FCSTD DOCUMENT  (FreeCAD 1.1R14555 (Git shallow))
Label: generated_example_K93-10436_all7
License: All rights reserved
LicenseURL: https://en.wikipedia.org/wiki/All_rights_reserved
objects: App::FeaturePython×7, App::Link×5, Assembly::JointGroup×1, Assembly::AssemblyObject×1, App::Point×1
EXTERNAL_REF file=K93-10436-H7-L120.FCStd obj=K93_120
EXTERNAL_REF file=Reference_all7.FCStd obj=Reference_all7_1
EXTERNAL_REF file=K93-10436-H7-L120_frontpanel_generated_example.FCStd obj=Body
EXTERNAL_REF file=K93-10436-H7-L120_Bumperino.FCStd obj=Body

FEATURE [App::Link] K93_120  label="K93-120"
  LinkPlacement = pos=(0,126.938,111.562) rot=(1,0,0;1.5708rad)
  LinkedObject = -> <external K93-10436-H7-L120.FCStd>#K93_120
  Placement = pos=(0,126.938,111.562) rot=(1,0,0;1.5708rad)
FEATURE [App::FeaturePython] GroundedJoint  # Assembly grounded joint (typed FeaturePython)
  ObjectToGround = -> K93_120
  Placement = pos=(0,126.938,111.562) rot=(1,0,0;1.5708rad)
FEATURE [App::Link] Reference_all7_1  label="Reference_all7 1"
  LinkPlacement = pos=(2.87919,6.93809,110.59) rot=(0.99808,0,0;0rad)
  LinkedObject = -> <external Reference_all7.FCStd>#Reference_all7_1
  Placement = pos=(2.87919,6.93809,110.59) rot=(0.99808,0,0;0rad)
FEATURE [App::FeaturePython] Joint  label="Distance"  # Assembly joint (typed FeaturePython)
  Angle = 0
  AngleMax = 0
  AngleMin = 0
  Detach1 = false
  Detach2 = false
  Distance = -0.2
  Distance2 = 0
  EnableAngleMax = false
  EnableAngleMin = false
  EnableLengthMax = false
  EnableLengthMin = false
  JointType = 5 (Distance)
  LengthMax = 0
  LengthMin = 0
  Offset1 = pos=(0,0,0) rot=(0,0,1;3.14159rad)
  Placement1 = pos=(-50,10.1,0) rot=(-0.707107,0,0.707107;3.14159rad)
  Placement2 = pos=(-49.8,1.8e-15,0.755) rot=(-0.57735,-0.57735,0.57735;2.0944rad)
  Reference1 = -> Assembly [K93_120.Part__Feature.Face87,K93_120.Part__Feature.Vertex159]
  Reference2 = -> Assembly [Reference_all7_1.Part__Feature426.Face3,Reference_all7_1.Part__Feature426.Vertex3]
  Suppressed = false
FEATURE [App::FeaturePython] Joint001  label="Distance001"  # Assembly joint (typed FeaturePython)
  Angle = 0
  AngleMax = 0
  AngleMin = 0
  Detach1 = false
  Detach2 = false
  Distance = 0.2
  Distance2 = 0
  EnableAngleMax = false
  EnableAngleMin = false
  EnableLengthMax = false
  EnableLengthMin = false
  JointType = 5 (Distance)
  LengthMax = 0
  LengthMin = 0
  Placement1 = pos=(4e-16,-59.8,0.755) rot=(0,-0.707107,0.707107;3.14159rad)
  Placement2 = pos=(1.58751,4.42551,60) rot=(0,0,1;0rad)
  Reference1 = -> Assembly [Reference_all7_1.Part__Feature426.Face1,Reference_all7_1.Part__Feature426.Vertex4]
  Reference2 = -> Assembly [K93_120.Part__Feature.Face58,K93_120.Part__Feature.Vertex116]
  Suppressed = false
FEATURE [App::FeaturePython] Joint002  label="Distance002"  # Assembly joint (typed FeaturePython)
  Angle = 0
  AngleMax = 0
  AngleMin = 0
  Detach1 = false
  Detach2 = false
  Distance = 0.25
  Distance2 = 0
  EnableAngleMax = false
  EnableAngleMin = false
  EnableLengthMax = false
  EnableLengthMin = false
  JointType = 5 (Distance)
  LengthMax = 0
  LengthMin = 0
  Placement1 = pos=(-48.85,11.1,0) rot=(-0.57735,-0.57735,0.57735;4.18879rad)
  Placement2 = pos=(0.0111337,0.109635,1.51) rot=(0,0,1;0rad)
  Reference1 = -> Assembly [K93_120.Part__Feature.Face78,K93_120.Part__Feature.Vertex160]
  Reference2 = -> Assembly [Reference_all7_1.Part__Feature426.Face5,Reference_all7_1.Part__Feature426.Vertex3]
  Suppressed = false
FEATURE [App::Link] Body
  LinkPlacement = pos=(2.87919,-53.8119,119.256) rot=(1,0,0;1.5708rad)
  LinkedObject = -> <external K93-10436-H7-L120_frontpanel_generated_example.FCStd>#Body
  Placement = pos=(2.87919,-53.8119,119.256) rot=(1,0,0;1.5708rad)
FEATURE [App::FeaturePython] Joint003  label="Fixed"  # Assembly joint (typed FeaturePython)
  Angle = 0
  AngleMax = 0
  AngleMin = 0
  Detach1 = false
  Detach2 = false
  Distance = 0
  Distance2 = 0
  EnableAngleMax = false
  EnableAngleMin = false
  EnableLengthMax = false
  EnableLengthMin = false
  JointType = 0 (Fixed)
  LengthMax = 0
  LengthMin = 0
  Offset2 = pos=(0,0,0) rot=(0,0,1;3.14159rad)
  Placement1 = pos=(9.8e-15,0,60) rot=(0.707107,0,0.707107;3.14159rad)
  Placement2 = pos=(1.5015e-12,17.9943,-0.75) rot=(0,1,0;4.71239rad)
  Reference1 = -> Assembly [K93_120.Part__Feature001.Edge190,K93_120.Part__Feature001.Edge190]
  Reference2 = -> Assembly [Body.Edge39,Body.Edge39]
  Suppressed = false
FEATURE [App::Link] Body001
  LinkPlacement = pos=(2.87919,-54.5619,119.256) rot=(1,0,0;1.5708rad)
  LinkedObject = -> <external K93-10436-H7-L120_Bumperino.FCStd>#Body
  Placement = pos=(2.87919,-54.5619,119.256) rot=(1,0,0;1.5708rad)
FEATURE [App::Link] Body002
  LinkPlacement = pos=(2.87919,-54.5619,119.256) rot=(0,0.707107,-0.707107;3.14159rad)
  LinkedObject = -> <external K93-10436-H7-L120_Bumperino.FCStd>#Body
  Placement = pos=(2.87919,-54.5619,119.256) rot=(0,0.707107,-0.707107;3.14159rad)
FEATURE [App::FeaturePython] Joint004  label="Fixed001"  # Assembly joint (typed FeaturePython)
  Angle = 0
  AngleMax = 0
  AngleMin = 0
  Detach1 = false
  Detach2 = false
  Distance = 0
  Distance2 = 0
  EnableAngleMax = false
  EnableAngleMin = false
  EnableLengthMax = false
  EnableLengthMin = false
  JointType = 0 (Fixed)
  LengthMax = 0
  LengthMin = 0
  Offset2 = pos=(0,0,0) rot=(0,0,1;3.14159rad)
  Placement1 = pos=(-52,0,0.75) rot=(-0.57735,-0.57735,0.57735;4.18879rad)
  Placement2 = pos=(-52,1.42e-14,7.1e-15) rot=(0.57735,-0.57735,-0.57735;4.18879rad)
  Reference1 = -> Assembly [Body.Edge13,Body.Edge13]
  Reference2 = -> Assembly [Body001.Edge19,Body001.Edge19]
  Suppressed = false
FEATURE [App::FeaturePython] Joint005  label="Fixed002"  # Assembly joint (typed FeaturePython)
  Angle = 0
  AngleMax = 0
  AngleMin = 0
  Detach1 = false
  Detach2 = false
  Distance = 0
  Distance2 = 0
  EnableAngleMax = false
  EnableAngleMin = false
  EnableLengthMax = false
  EnableLengthMin = false
  JointType = 0 (Fixed)
  LengthMax = 0
  LengthMin = 0
  Placement1 = pos=(52,5.9828e-12,0.75) rot=(0.57735,0.57735,0.57735;4.18879rad)
  Placement2 = pos=(-52,0,0) rot=(0.57735,0.57735,0.57735;4.18879rad)
  Reference1 = -> Assembly [Body.Edge16,Body.Edge16]
  Reference2 = -> Assembly [Body002.Edge19,Body002.Edge19]
  Suppressed = false
FEATURE [Assembly::JointGroup] Joints
  Group = -> [GroundedJoint,Joint,Joint001,Joint002,Joint003,Joint004,Joint005]
FEATURE [Assembly::AssemblyObject] Assembly
  Group = -> [Joints,K93_120,GroundedJoint,Reference_all7_1,Joint,Joint001,Joint002,Body,Joint003,Body001,Body002,Joint004,Joint005]
  Origin = -> Origin
  Type = Assembly
FEATURE [App::Point] Origin001  label="Origin"
  Role = Origin

RESOLVED EXTERNAL PARTS (link-assembly join: the EXTERNAL_REF files above that resolve inside this repo's crawl, each included once):
---- part K93-10436-H7-L120_Bumperino.FCStd = doc fcstd_554f42e3a84f ----
FCSTD DOCUMENT  (FreeCAD 1.0R39319 (Git))
Label: K93-10436-H7-L120_Bumperino
License: All rights reserved
LicenseURL: https://en.wikipedia.org/wiki/All_rights_reserved
objects: Part::Feature×5, Sketcher::SketchObject×3, PartDesign::Pocket×2, App::DocumentObjectGroupPython×1, PartDesign::Pad×1, PartDesign::Mirrored×1, PartDesign::Body×1
note: 23 computed .brp shape members not serialized (recipe doc carries the construction recipe); baked Part::Feature solids carry a one-line shape summary decoded from their .brp

FEATURE [App::DocumentObjectGroupPython] LayerContainer  label="Layers"  # scripted group (container) (typed FeaturePython)
FEATURE [Part::Feature] Wire
  shape: bbox 3.2 x 3.2 x 2e-07 mm, 0 faces, 0 solids (baked)
FEATURE [Part::Feature] Wire001
  shape: bbox 3.2 x 3.2 x 2e-07 mm, 0 faces, 0 solids (baked)
FEATURE [Part::Feature] Wire002
  shape: bbox 3.2 x 3.2 x 2e-07 mm, 0 faces, 0 solids (baked)
FEATURE [Part::Feature] Wire003
  shape: bbox 3.2 x 3.2 x 2e-07 mm, 0 faces, 0 solids (baked)
FEATURE [Part::Feature] Wire004  label="PanelConture"
  shape: bbox 104 x 35.99 x 2e-07 mm, 0 faces, 0 solids (baked)
FEATURE [Sketcher::SketchObject] Sketch
  ArcFitTolerance = 1e-06
  FullyConstrained = true
  MakeInternals = false
  sketch-geometry (12):
    g0: ArcOfCircle CenterX=-46.1716 CenterY=15.9943 CenterZ=0 NormalX=0 NormalY=0 NormalZ=1 AngleXU=0 Radius=1.99973 StartAngle=1.5708 EndAngle=2.35633
    g1: LineSegment StartX=-47.5858 StartY=17.4081 StartZ=0 EndX=-51.4142 EndY=13.5801 EndZ=0
    g2: ArcOfCircle CenterX=-50 CenterY=12.1658 CenterZ=0 NormalX=0 NormalY=0 NormalZ=1 AngleXU=0 Radius=2 StartAngle=2.35619 EndAngle=3.14159
    g3: ArcOfCircle CenterX=-46.1716 CenterY=15.3778 CenterZ=0 NormalX=0 NormalY=0 NormalZ=1 AngleXU=0 Radius=2.6162 StartAngle=0.0358549 EndAngle=1.5708
    g4: LineSegment StartX=-43.5571 StartY=15.4716 StartZ=0 EndX=-43.3913 EndY=10.8516 EndZ=0
    g5: ArcOfCircle CenterX=-45.8905 CenterY=10.7619 CenterZ=0 NormalX=0 NormalY=0 NormalZ=1 AngleXU=0 Radius=2.50074 StartAngle=5.05273 EndAngle=6.31904
    g6: LineSegment StartX=-45.0557 StartY=8.40462 StartZ=0 EndX=-49.3762 EndY=6.87461 EndZ=0
    g7: ArcOfCircle CenterX=-48.9841 CenterY=5.76738 CenterZ=0 NormalX=0 NormalY=0 NormalZ=1 AngleXU=0 Radius=1.17461 StartAngle=1.91114 EndAngle=3.14159
    g8: LineSegment StartX=-50.1587 StartY=5.76738 StartZ=0 EndX=-50.1587 EndY=0 EndZ=0
    g9: LineSegment StartX=-50.1587 StartY=0 StartZ=0 EndX=-52 EndY=0 EndZ=0
    g10: LineSegment StartX=-52 StartY=12.1658 StartZ=0 EndX=-52 EndY=0 EndZ=0
    g11: Circle CenterX=-47.3 CenterY=11.9443 CenterZ=0 NormalX=0 NormalY=0 NormalZ=1 AngleXU=0 Radius=1.6
  constraints (22):
    c: Coincident(g0,g1)
    c: Coincident(g1,g2)
    c: Block(g0)
    c: Block(g1)
    c: Block(g2)
    c: PointOnObject(g8,g-1)
    c: Tangent(g7,g6) = -1.5708
    c: Tangent(g8,g7) = -1.5708
    c: Tangent(g6,g5) = 1.5708
    c: Tangent(g5,g4) = 1.5708
    c: Tangent(g4,g3) = 1.5708
    c: Coincident(g9,g8)
    c: Horizontal(g9)
    c: Tangent(g10,g2) = -1.5708
    c: Coincident(g10,g9)
    c: Vertical(g10)
    c: Block(g10)
    c: Block(g7)
    c: Block(g5)
    c: Tangent(g0,g3) = -1.5708
    c: Block(g3)
    c: Block(g11)
FEATURE [PartDesign::Pad] Pad  label="LengthBumper"
  Direction = (0,0,1)
  Length = 20
  Length2 = 10
  Profile = -> Sketch
  ReferenceAxis = -> Sketch [N_Axis]
  Refine = true
  Suppressed = false
  Type = 0
FEATURE [PartDesign::Mirrored] Mirrored
  BaseFeature = -> Pad
  MirrorPlane = -> Sketch [H_Axis]
  Originals = -> [Pad]
  Refine = true
  Suppressed = false
  TransformMode = 0
FEATURE [Sketcher::SketchObject] Sketch001
  ArcFitTolerance = 1e-06
  AttachmentSupport = -> [Mirrored]
  ExternalGeometry = -> [Mirrored]
  FullyConstrained = true
  MakeInternals = false
  MapMode = 5
  Placement = pos=(0,0,20) rot=(0,0,1;0rad)
  sketch-geometry (2):
    g0: Circle CenterX=-47.3 CenterY=11.9443 CenterZ=0 NormalX=0 NormalY=0 NormalZ=1 AngleXU=0 Radius=3
    g1: Circle CenterX=-47.3 CenterY=-11.9443 CenterZ=0 NormalX=0 NormalY=0 NormalZ=1 AngleXU=0 Radius=3
  constraints (4):
    c: Coincident(g0,g-3)
    c: Coincident(g1,g-4)
    c: Diameter(g1) = 6
    c: Equal(g0,g1)
FEATURE [PartDesign::Pocket] Pocket
  BaseFeature = -> Mirrored
  Direction = (0,0,-1)
  Length = 0
  Length2 = 5
  Offset = 5
  Profile = -> Sketch001
  ReferenceAxis = -> Sketch001 [N_Axis]
  Refine = true
  Suppressed = false
  Type = 3
  UpToFace = -> Mirrored [Face9]
FEATURE [Sketcher::SketchObject] Sketch002
  ArcFitTolerance = 1e-06
  AttachmentSupport = -> [XZ_Plane]
  ExternalGeometry = -> [Pocket]
  FullyConstrained = true
  MakeInternals = false
  MapMode = 5
  Placement = pos=(0,0,0) rot=(1,0,0;1.5708rad)
  sketch-geometry (3):
    g0: LineSegment StartX=-43.3913 StartY=20 StartZ=0 EndX=-52 EndY=20 EndZ=0
    g1: LineSegment StartX=-52 StartY=20 StartZ=0 EndX=-52 EndY=11.3914 EndZ=0
    g2: ArcOfCircle CenterX=-43.3913 CenterY=11.3913 CenterZ=0 NormalX=0 NormalY=0 NormalZ=1 AngleXU=0 Radius=8.60867 StartAngle=1.5708 EndAngle=3.14159
  constraints (8):
    c: Coincident(g0,g-3)
    c: Coincident(g0,g-5)
    c: Coincident(g1,g0)
    c: PointOnObject(g1,g-5)
    c: PointOnObject(g2,g-6)
    c: Coincident(g2,g1)
    c: Coincident(g2,g0)
    c: Tangent(g2,g-5)
FEATURE [PartDesign::Pocket] Pocket001
  BaseFeature = -> Pocket
  Direction = (0,1,-2e-16)
  Length = 5
  Length2 = 5
  Midplane = true
  Profile = -> Sketch002
  ReferenceAxis = -> Sketch002 [N_Axis]
  Refine = true
  Suppressed = false
  Type = 1
FEATURE [PartDesign::Body] Body
  AllowCompound = false
  Group = -> [Sketch,Pad,Mirrored,Sketch001,Pocket,Sketch002,Pocket001]
  Origin = -> Origin
  Placement = pos=(0,0,0) rot=(1,0,0;1.5708rad)
  Tip = -> Pocket001
---- part K93-10436-H7-L120_frontpanel_generated_example.FCStd = doc fcstd_f3005fab9b42 ----
FCSTD DOCUMENT  (FreeCAD 1.1R14555 (Git shallow))
Label: K93-10436-H7-L120_frontpanel_generated_example
License: All rights reserved
LicenseURL: https://en.wikipedia.org/wiki/All_rights_reserved
objects: Part::Feature×1, PartDesign::FeatureBase×1, Sketcher::SketchObject×1, PartDesign::Pocket×1, PartDesign::Body×1, App::Point×1
note: 9 computed .brp shape members not serialized (recipe doc carries the construction recipe); baked Part::Feature solids carry a one-line shape summary decoded from their .brp

FEATURE [Part::Feature] Part__Feature  label="K93-B"
  shape: bbox 104 x 35.99 x 1.5 mm, 34 faces (baked)
FEATURE [PartDesign::FeatureBase] BaseFeature
  BaseFeature = -> Part__Feature
  Suppressed = false
FEATURE [Sketcher::SketchObject] Sketch
  ArcFitTolerance = 1e-06
  AttachmentSupport = -> [BaseFeature]
  ExternalTypes = [0]
  FullyConstrained = false
  MakeInternals = false
  MapMode = 5
  Placement = pos=(0,0,0.75) rot=(0,0,1;0rad)
  sketch-geometry (7):
    g0: Circle CenterX=-40.64 CenterY=2.6 CenterZ=0 NormalX=0 NormalY=0 NormalZ=1 AngleXU=0 Radius=3.15
    g1: Circle CenterX=-26.66 CenterY=2.72 CenterZ=0 NormalX=0 NormalY=0 NormalZ=1 AngleXU=0 Radius=6.5
    g2: Circle CenterX=-11.43 CenterY=1.92 CenterZ=0 NormalX=0 NormalY=0 NormalZ=1 AngleXU=0 Radius=5.75
    g3: Circle CenterX=1.29 CenterY=-0.88 CenterZ=0 NormalX=0 NormalY=0 NormalZ=1 AngleXU=0 Radius=1.8
    g4: Circle CenterX=13.97 CenterY=0.62 CenterZ=0 NormalX=0 NormalY=0 NormalZ=1 AngleXU=0 Radius=3.5
    g5: Circle CenterX=26.67 CenterY=2.6 CenterZ=0 NormalX=0 NormalY=0 NormalZ=1 AngleXU=0 Radius=3.15
    g6: Circle CenterX=35.56 CenterY=-1.85 CenterZ=0 NormalX=0 NormalY=0 NormalZ=1 AngleXU=0 Radius=2.6
FEATURE [PartDesign::Pocket] Pocket
  BaseFeature = -> BaseFeature
  Direction = (0,0,-1)
  Length = 5
  Length2 = 5
  Profile = -> Sketch
  ReferenceAxis = -> Sketch [N_Axis]
  Refine = true
  SideType = 0
  Suppressed = false
  Type = 1
  Type2 = 0
FEATURE [PartDesign::Body] Body
  AllowCompound = false
  BaseFeature = -> Part__Feature
  Group = -> [BaseFeature,Sketch,Pocket]
  Origin = -> Origin
  Tip = -> Pocket
FEATURE [App::Point] Origin001  label="Origin"
  Role = Origin
